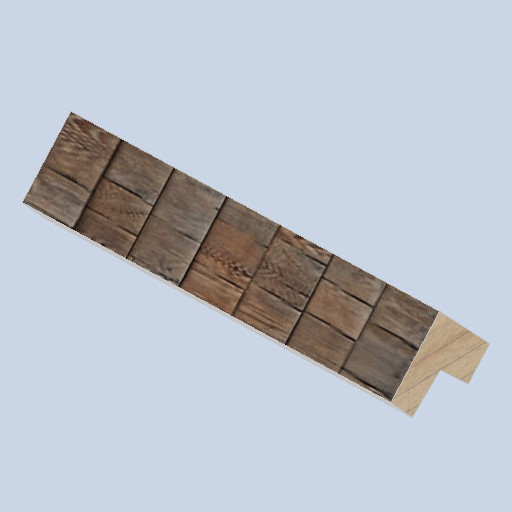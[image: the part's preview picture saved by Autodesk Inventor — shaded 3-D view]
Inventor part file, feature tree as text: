
AUTODESK INVENTOR PART (.ipt)
format: ipt  version: 2024.2 (Build 282272000, 272)  size: 244,224 bytes
history: native  units: in
note: dims shown in document units (in); Inventor stores cm internally (conversion verified against a paired STEP export)
features: sketch x8, plane x6, other x3
ambient origin geometry x8: Origin, YZ Plane, XZ Plane, XY Plane, X Axis, Y Axis, Z Axis, Center Point
bodies: Solid1 (feature_tree)
feature tree (17):
  other  "panel_pad_frame_01_MIR.ipt"
  other  "Solid1::panel_pad_frame_01_MIR.ipt"
  other  "TaggingFeature1"
  sketch  "Sketch1"  dims[d0=0.3937in]
  sketch  "Sketch2"
  sketch  "Sketch3"
  sketch  "Sketch6"
  sketch  "Sketch7"
  sketch  "Sketch8"
  sketch  "Sketch9"
  sketch  "Sketch10"
  plane  "Work Plane1"
  plane  "Work Plane2"
  plane  "Work Plane3"
  plane  "Work Plane4"
  plane  "Work Plane5"
  plane  "Work Plane6"
